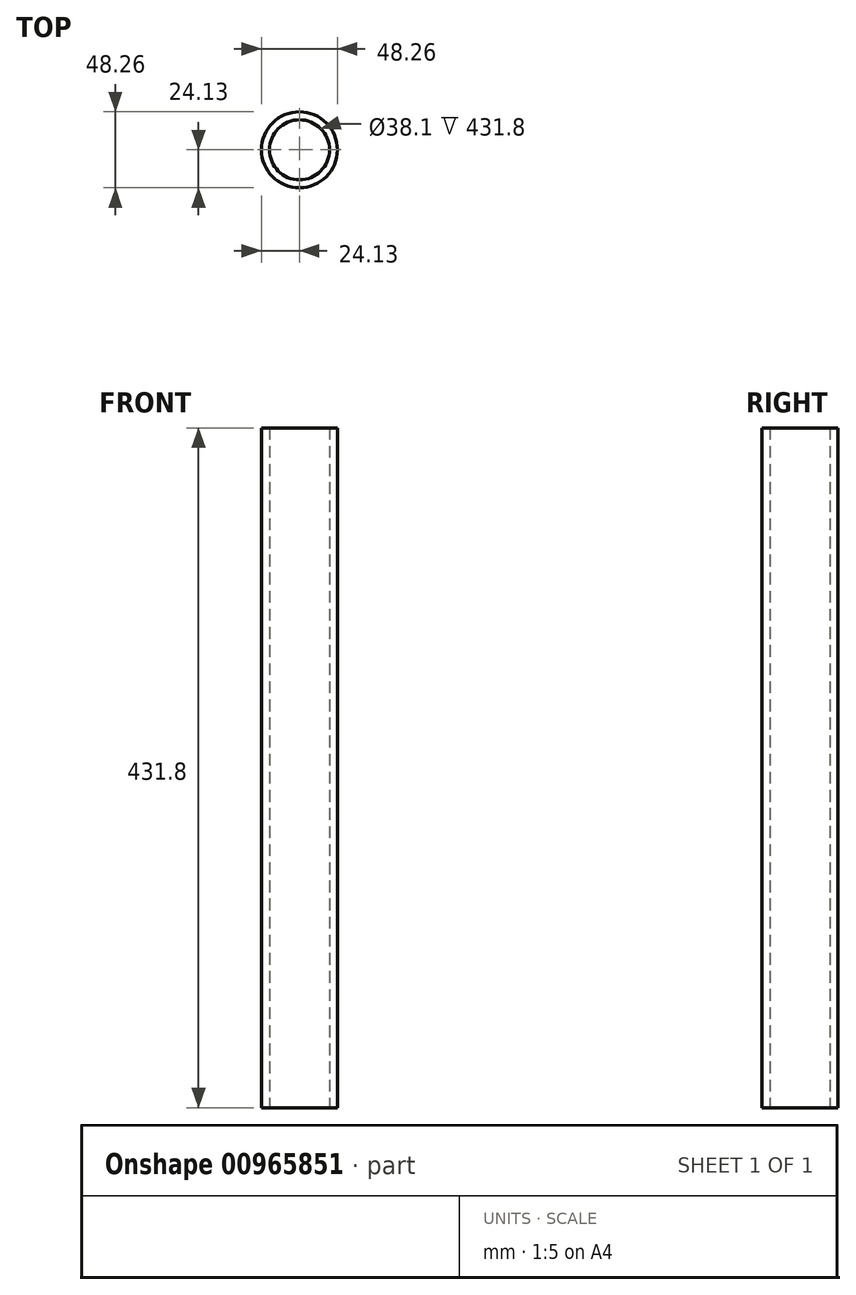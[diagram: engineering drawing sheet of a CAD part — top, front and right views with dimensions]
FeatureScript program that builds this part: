
annotation { "Feature Type Name" : "Feature", "Feature Type Description" : "" }
export const myFeature = defineFeature(function(context is Context, id is Id, definition is map)
    precondition{}
    {
        {
            var Q0;
            Q0=qCreatedBy(makeId("Top.planeOp"),FACE);
            var sketch = newSketch(context, id + "F0", { "sketchPlane" : qUnion([Q0])});
            skCircle(sketch, "E0", {"center": v(0, 0) * mm, "radius": 19.05 * mm});
            skCircle(sketch, "E1", {"center": v(0, 0) * mm, "radius": 24.13 * mm});
            skSolve(sketch);
        }
        {
            var Q0;
            Q0=makeQuery(id+"F0.imprint","IMPRINT",FACE,{"disambiguationData":[TD([[makeQuery(id+"F0.imprint","IMPRINT",EDGE,{"derivedFrom":sQuery(id+"F0.wireOp",EDGE,"E0")}),-1.0]])]});
            extrude(context, id + "F1", {"entities" : qUnion([Q0]), "depth" : 431.8 * mm, "offsetDistance" : 25.4 * mm});
        }
    });
